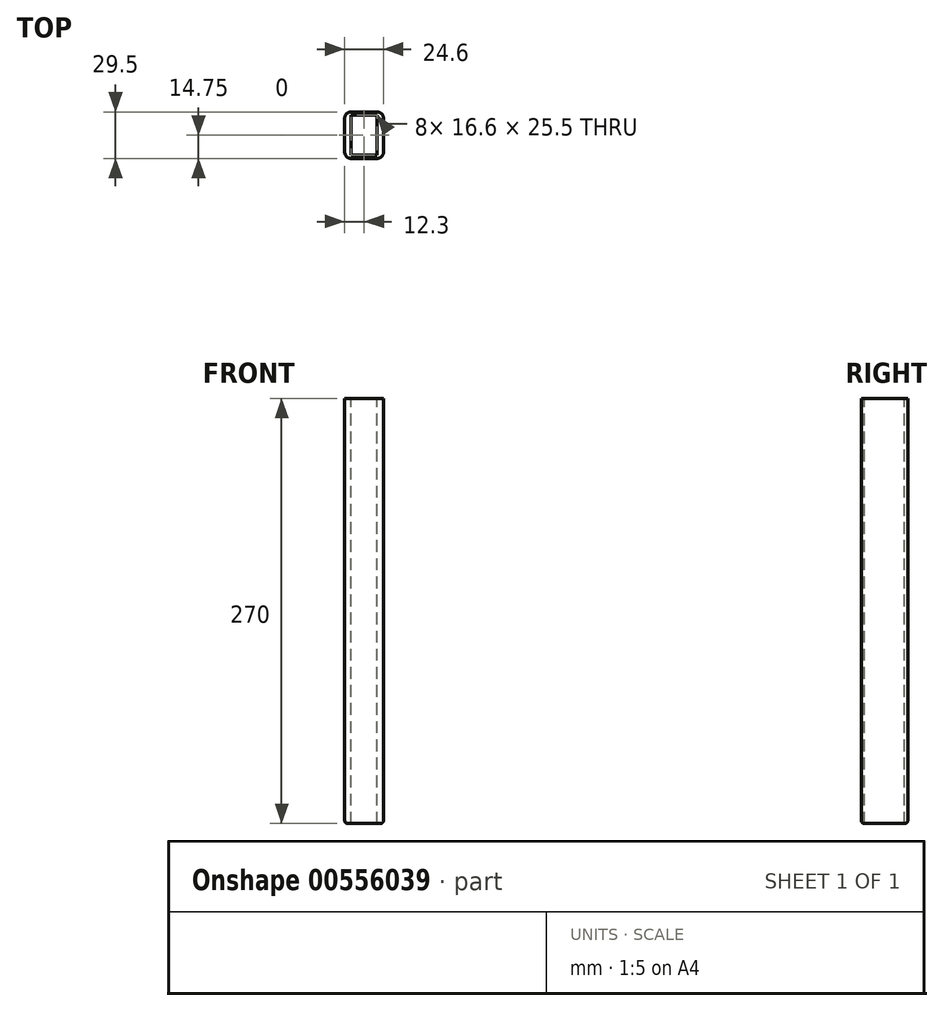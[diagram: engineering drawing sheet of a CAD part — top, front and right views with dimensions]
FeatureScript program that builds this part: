
annotation { "Feature Type Name" : "Feature", "Feature Type Description" : "" }
export const myFeature = defineFeature(function(context is Context, id is Id, definition is map)
    precondition{}
    {
        {
            var Q0;
            Q0=qCreatedBy(makeId("Top.planeOp"),FACE);
            var sketch = newSketch(context, id + "F0", { "sketchPlane" : qUnion([Q0])});
            skLineSegment(sketch, "E0.bottom", {"start": v(-12.3, -14.75) * mm, "end": v(12.3, -14.75) * mm});
            skLineSegment(sketch, "E0.top", {"start": v(-12.3, 14.75) * mm, "end": v(12.3, 14.75) * mm});
            skLineSegment(sketch, "E0.left", {"start": v(-12.3, -14.75) * mm, "end": v(-12.3, 14.75) * mm});
            skLineSegment(sketch, "E0.right", {"start": v(12.3, -14.75) * mm, "end": v(12.3, 14.75) * mm});
            skPoint(sketch, "E0.middle", {"position": v(0, 0) * mm});
            skLineSegment(sketch, "E1.bottom", {"start": v(-8.3, -12.75) * mm, "end": v(8.3, -12.75) * mm});
            skLineSegment(sketch, "E1.top", {"start": v(-8.3, 12.75) * mm, "end": v(8.3, 12.75) * mm});
            skLineSegment(sketch, "E1.left", {"start": v(-8.3, -12.75) * mm, "end": v(-8.3, 12.75) * mm});
            skLineSegment(sketch, "E1.right", {"start": v(8.3, -12.75) * mm, "end": v(8.3, 12.75) * mm});
            skPoint(sketch, "E2", {"position": v(0, -12.75) * mm});
            skPoint(sketch, "E3", {"position": v(-8.3, 0) * mm});
            skSolve(sketch);
        }
        {
            var Q0;
            Q0=makeQuery(id+"F0.imprint","IMPRINT",FACE,{"disambiguationData":[TD([[makeQuery(id+"F0.imprint","IMPRINT",EDGE,{"derivedFrom":sQuery(id+"F0.wireOp",EDGE,"E0.bottom")}),1.0]])]});
            extrude(context, id + "F1", {"entities" : qUnion([Q0]), "oppositeDirection" : true, "depth" : 270 * mm, "offsetDistance" : 25 * mm});
        }
        {
            var Q0;
            Q0=makeQuery(id+"F1.opExtrude","CAP_EDGE",EDGE,{"disambiguationData":[OSD([sQuery(id+"F0.wireOp",EDGE,"E0.left")])],"isStart":false});
            var Q1;
            Q1=makeQuery(id+"F1.opExtrude","CAP_EDGE",EDGE,{"disambiguationData":[OSD([sQuery(id+"F0.wireOp",EDGE,"E0.top")])],"isStart":false});
            var Q2;
            Q2=makeQuery(id+"F1.opExtrude","CAP_EDGE",EDGE,{"disambiguationData":[OSD([sQuery(id+"F0.wireOp",EDGE,"E0.right")])],"isStart":false});
            var Q3;
            Q3=makeQuery(id+"F1.opExtrude","CAP_EDGE",EDGE,{"disambiguationData":[OSD([sQuery(id+"F0.wireOp",EDGE,"E0.bottom")])],"isStart":false});
            fillet(context, id + "F2", {"entities" : qUnion([Q0, Q1, Q2, Q3]), "radius" : 2 * mm, "tangentPropagation" : true, "allowEdgeOverflow" : false});
        }
        {
            var Q0;
            Q0=makeQuery(id+"F1.opExtrude","SWEPT_EDGE",EDGE,{"disambiguationData":[OSD([sQuery(id+"F0.wireOp",EDGE,"E0.top"),sQuery(id+"F0.wireOp",EDGE,"E0.right")])]});
            var Q1;
            Q1=makeQuery(id+"F1.opExtrude","SWEPT_EDGE",EDGE,{"disambiguationData":[OSD([sQuery(id+"F0.wireOp",EDGE,"E0.top"),sQuery(id+"F0.wireOp",EDGE,"E0.left")])]});
            var Q2;
            Q2=makeQuery(id+"F1.opExtrude","SWEPT_EDGE",EDGE,{"disambiguationData":[OSD([sQuery(id+"F0.wireOp",EDGE,"E0.bottom"),sQuery(id+"F0.wireOp",EDGE,"E0.right")])]});
            var Q3;
            Q3=makeQuery(id+"F1.opExtrude","SWEPT_EDGE",EDGE,{"disambiguationData":[OSD([sQuery(id+"F0.wireOp",EDGE,"E0.bottom"),sQuery(id+"F0.wireOp",EDGE,"E0.left")])]});
            fillet(context, id + "F3", {"entities" : qUnion([Q0, Q1, Q2, Q3]), "radius" : 4 * mm, "tangentPropagation" : true, "allowEdgeOverflow" : false});
        }
    });
